# Revit family: Bubbler - 1400 Series
name_source: partatom
category: Conexões de tubo
units: mm (PartAtom-declared; Revit-internal decimal feet)

## family parameters
Com base no plano de trabalho = Sim
Compartilhado = Não
Corte com vazios quando carregada = Não
Cota do conector redondo = Utilizar diâmetro
Número OmniClass = 23.60.30.11.14
Sempre na vertical = Sim
Tipo de parte = Cobertura
Título OmniClass = Pipework Fittings

## types (4) — shared parameters
Aluminum = Aluminum
Cover = Black Plastic
DT1 = 0 ft
DT12 = 0 ft
DT13 = 0 ft
DT2 = 0 ft
DT6 = 0 ft
Descrição = Spray Nozzles 1400 Series
Elevação-padrão = 4 ft
H2 = 1 ft
Plastic = Plastic Black
RainBird: Product Link = https://store.rainbird.com
Reviw = R01
SupportProjetos: Level of Detail = LOD 300
SupportProjetos: Reviw Date = 26/03/2021
URL = https://www.rainbird.com
Water = Water
Water Visibility (Circle) = Sim

## per-type parameters (varying)
| type | Angle | Flow |
| 1401 | 5.00° | 0.3 gal/min |
| 1402 | 5.00° | 0.5 gal/min |
| 1404 | 5.00° | 1.0 gal/min |
| 1408 | 10.00° | 2.0 gal/min |

note: column(s) folded — value = type name in every type: Modelo
